# Revit family: FireFighting_Firemain-Booster-Hydrant-Suction-Riser-Set_Galvin_150TE
name_source: partatom
category: Mechanical Equipment
revit_build: Autodesk Revit MEP 2012 (Build: 20110916_2132(x64)
units: mm (PartAtom-declared; Revit-internal decimal feet)

## types (2) — shared parameters
Assembly Code = D4030
DimDepth = 600 mm
DimHeight = 1500 mm  [stored 4.92126 ft]
DimInletRadius = 50 mm  [stored 0.164042 ft]
FlowRate = 0.00 L/s
Instructions = http://www.galvinengineering.com.au
Keynote = 10520
Manufacturer = Galvin Engineering
ModifiedIssue_ANZRS = 20140330 $
StyleOrType_ANZRS = Fire Fighting Equipment
URL = www.galvinengineering.com.au

## per-type parameters (varying)
| type | Description | DimWidth |
| 380139 | WA/NT Firemain Booster & Hydrant Set 150TE [No Suction Riser] with Cabinet (Painted) | 2000 mm  [stored 6.56168 ft] |
| 380139SR | WA/NT Firemain Booster, Hydrant & Suction Riser Set 150TE with Cabinet (Painted) | 2400 mm |

note: column(s) folded — value = type name in every type: FilterObject_ANZRS, Model, Type Comments

note: [stored X ft] marks values corroborated as IEEE doubles in the binary element streams (Revit-internal decimal feet)

## geometry (parser evidence)
native form markers: Blend x4, Sweep x1
no freeform markers — native parametric forms only
